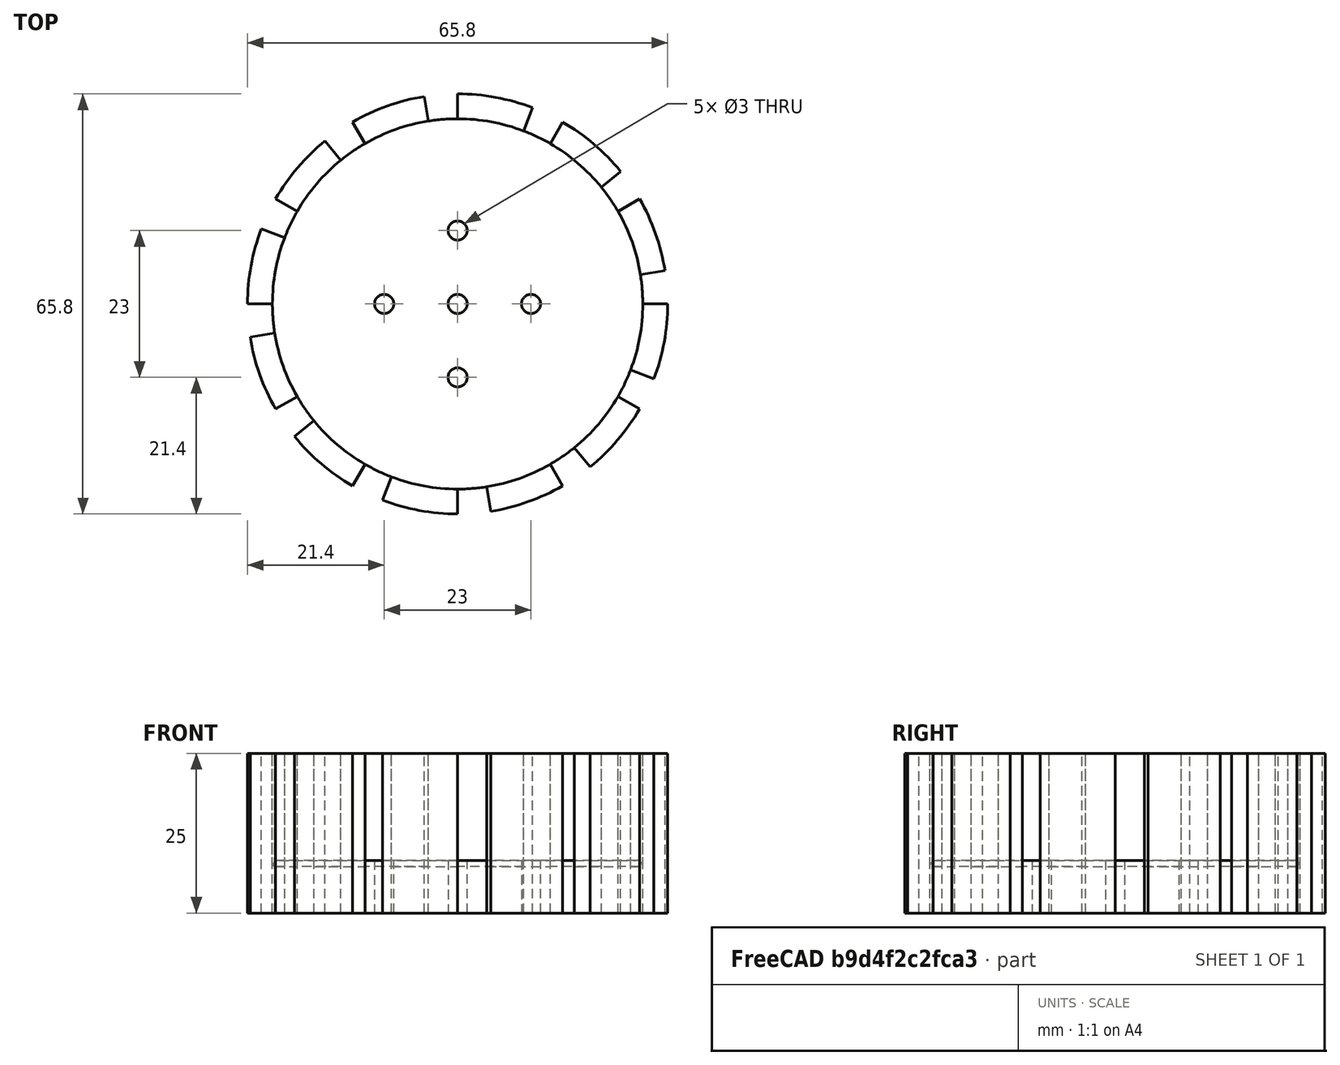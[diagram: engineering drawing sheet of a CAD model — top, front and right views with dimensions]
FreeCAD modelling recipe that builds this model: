
FCSTD DOCUMENT  (FreeCAD 1.0R39109 (Git))
Label: wheel
License: CERN Open Hardware Licence weakly-reciprocal
LicenseURL: https://cern-ohl.web.cern.ch/
objects: TechDraw::DrawViewDimension×3, Sketcher::SketchObject×2, PartDesign::Pad×2, PartDesign::Body×2, TechDraw::DrawProjGroupItem×2, TechDraw::DrawSVGTemplate×1, TechDraw::DrawViewImage×1, PartDesign::Fillet×1, PartDesign::Boolean×1, App::Part×1, TechDraw::DrawProjGroup×1, TechDraw::DrawViewSection×1, TechDraw::DrawPage×1
note: 20 computed .brp shape members not serialized (recipe doc carries the construction recipe); baked Part::Feature solids carry a one-line shape summary decoded from their .brp

FEATURE [Sketcher::SketchObject] Sketch
  ArcFitTolerance = 1e-06
  AttachmentSupport = -> [XY_Plane001]
  FullyConstrained = true
  MakeInternals = false
  MapMode = 5
  sketch-geometry (10):
    g0: Circle CenterX=0 CenterY=0 CenterZ=0 NormalX=0 NormalY=0 NormalZ=1 AngleXU=0 Radius=29
    g1: Circle CenterX=0 CenterY=0 CenterZ=0 NormalX=0 NormalY=0 NormalZ=1 AngleXU=0 Radius=1.5
    g2: LineSegment [constr] StartX=0 StartY=0 StartZ=0 EndX=0 EndY=11.5 EndZ=0
    g3: LineSegment [constr] StartX=0 StartY=0 StartZ=0 EndX=11.5 EndY=0 EndZ=0
    g4: LineSegment [constr] StartX=0 StartY=0 StartZ=0 EndX=0 EndY=-11.5 EndZ=0
    g5: LineSegment [constr] StartX=0 StartY=0 StartZ=0 EndX=-11.5 EndY=0 EndZ=0
    g6: Circle CenterX=0 CenterY=11.5 CenterZ=0 NormalX=0 NormalY=0 NormalZ=1 AngleXU=0 Radius=1.5
    g7: Circle CenterX=11.5 CenterY=0 CenterZ=0 NormalX=0 NormalY=0 NormalZ=1 AngleXU=0 Radius=1.5
    g8: Circle CenterX=0 CenterY=-11.5 CenterZ=0 NormalX=0 NormalY=0 NormalZ=1 AngleXU=0 Radius=1.5
    g9: Circle CenterX=-11.5 CenterY=0 CenterZ=0 NormalX=0 NormalY=0 NormalZ=1 AngleXU=0 Radius=1.5
  constraints (26):
    c: Coincident(g0,g-1)
    c: Coincident(g1,g0)
    c: Diameter(g0) = 58
    c: Diameter(g1) = 3
    c: Block(g0)
    c: Block(g1)
    c: Coincident(g2,g0)
    c: PointOnObject(g2,g-2)
    c: Coincident(g3,g0)
    c: PointOnObject(g3,g-1)
    c: Coincident(g4,g0)
    c: PointOnObject(g4,g-2)
    c: Coincident(g5,g0)
    c: PointOnObject(g5,g-1)
    c: Equal(g5,g2)
    c: Equal(g3,g2)
    c: Equal(g4,g2)
    c: DistanceX(g5,g5) = 11.5
    c: Diameter(g6) = 3
    c: Coincident(g6,g2)
    c: Diameter(g7) = 3
    c: Coincident(g7,g3)
    c: Diameter(g8) = 3
    c: Coincident(g8,g4)
    c: Diameter(g9) = 3
    c: Coincident(g9,g5)
FEATURE [PartDesign::Pad] Pad
  Direction = (0,0,1)
  Length = 8.25
  Length2 = 10
  Profile = -> Sketch
  ReferenceAxis = -> Sketch [N_Axis]
  Suppressed = false
  Type = 0
FEATURE [Sketcher::SketchObject] Sketch004
  ArcFitTolerance = 1e-06
  FullyConstrained = false
  MakeInternals = false
  MapMode = 5
  sketch-geometry (50):
    g0: Circle [constr] CenterX=0 CenterY=0 CenterZ=0 NormalX=0 NormalY=0 NormalZ=1 AngleXU=0 Radius=32.9
    g1: Circle [constr] CenterX=0 CenterY=0 CenterZ=0 NormalX=0 NormalY=0 NormalZ=1 AngleXU=0 Radius=29
    g2: ArcOfCircle CenterX=0 CenterY=9.7e-15 CenterZ=0 NormalX=0 NormalY=0 NormalZ=1 AngleXU=0 Radius=32.9 StartAngle=5.91825 EndAngle=6.28319
    g3: ArcOfCircle CenterX=0 CenterY=9.7e-15 CenterZ=0 NormalX=0 NormalY=0 NormalZ=1 AngleXU=0 Radius=29 StartAngle=5.91825 EndAngle=6.28319
    g4: LineSegment StartX=29 StartY=-2.32e-14 StartZ=0 EndX=32.9 EndY=-2.32e-14 EndZ=0
    g5: LineSegment StartX=27.0903 StartY=-10.3497 StartZ=0 EndX=30.7335 EndY=-11.7415 EndZ=0
    g6: ArcOfCircle CenterX=-3.69141e-06 CenterY=0 CenterZ=0 NormalX=0 NormalY=0 NormalZ=1 AngleXU=0 Radius=29 StartAngle=0.158668 EndAngle=0.523599
    g7: LineSegment StartX=25.1147 StartY=14.5 StartZ=0 EndX=28.4922 EndY=16.45 EndZ=0
    g8: ArcOfCircle CenterX=-3.69141e-06 CenterY=0 CenterZ=0 NormalX=0 NormalY=0 NormalZ=1 AngleXU=0 Radius=32.9 StartAngle=0.158668 EndAngle=0.523599
    g9: LineSegment StartX=28.6357 StartY=4.58208 StartZ=0 EndX=32.4867 EndY=5.1983 EndZ=0
    g10: ArcOfCircle CenterX=0 CenterY=7.38281e-06 CenterZ=0 NormalX=0 NormalY=0 NormalZ=1 AngleXU=0 Radius=29 StartAngle=0.682267 EndAngle=1.0472
    g11: LineSegment StartX=14.5 StartY=25.1147 StartZ=0 EndX=16.45 EndY=28.4922 EndZ=0
    g12: ArcOfCircle CenterX=0 CenterY=7.38281e-06 CenterZ=0 NormalX=0 NormalY=0 NormalZ=1 AngleXU=0 Radius=32.9 StartAngle=0.682266 EndAngle=1.0472
    g13: LineSegment StartX=22.5082 StartY=18.2861 StartZ=0 EndX=25.5352 EndY=20.7452 EndZ=0
    g14: ArcOfCircle CenterX=0 CenterY=1.755e-12 CenterZ=0 NormalX=0 NormalY=0 NormalZ=1 AngleXU=0 Radius=29 StartAngle=1.20587 EndAngle=1.5708
    g15: LineSegment StartX=9.47705e-06 StartY=29 StartZ=0 EndX=1.07516e-05 EndY=32.9 EndZ=0
    g16: ArcOfCircle CenterX=0 CenterY=1.755e-12 CenterZ=0 NormalX=0 NormalY=0 NormalZ=1 AngleXU=0 Radius=32.9 StartAngle=1.20587 EndAngle=1.5708
    g17: LineSegment StartX=10.3497 StartY=27.0903 StartZ=0 EndX=11.7415 EndY=30.7335 EndZ=0
    g18: ArcOfCircle CenterX=0 CenterY=1.68437e-06 CenterZ=0 NormalX=0 NormalY=0 NormalZ=1 AngleXU=0 Radius=29 StartAngle=1.72946 EndAngle=2.0944
    g19: LineSegment StartX=-14.5 StartY=25.1147 StartZ=0 EndX=-16.45 EndY=28.4922 EndZ=0
    g20: ArcOfCircle CenterX=0 CenterY=1.68437e-06 CenterZ=0 NormalX=0 NormalY=0 NormalZ=1 AngleXU=0 Radius=32.9 StartAngle=1.72946 EndAngle=2.0944
    g21: LineSegment StartX=-4.58208 StartY=28.6357 StartZ=0 EndX=-5.1983 EndY=32.4867 EndZ=0
    g22: ArcOfCircle CenterX=-2.15492e-07 CenterY=0 CenterZ=0 NormalX=0 NormalY=0 NormalZ=1 AngleXU=0 Radius=29 StartAngle=2.25306 EndAngle=2.61799
    g23: LineSegment StartX=-25.1147 StartY=14.5 StartZ=0 EndX=-28.4922 EndY=16.45 EndZ=0
    g24: ArcOfCircle CenterX=-2.15492e-07 CenterY=0 CenterZ=0 NormalX=0 NormalY=0 NormalZ=1 AngleXU=0 Radius=32.9 StartAngle=2.25306 EndAngle=2.61799
    g25: LineSegment StartX=-18.2861 StartY=22.5082 StartZ=0 EndX=-20.7452 EndY=25.5352 EndZ=0
    g26: ArcOfCircle CenterX=0 CenterY=0 CenterZ=0 NormalX=0 NormalY=0 NormalZ=1 AngleXU=0 Radius=29 StartAngle=2.77666 EndAngle=3.14159
    g27: LineSegment StartX=-29 StartY=1.124e-12 StartZ=0 EndX=-32.9 EndY=4e-15 EndZ=0
    g28: ArcOfCircle CenterX=0 CenterY=0 CenterZ=0 NormalX=0 NormalY=0 NormalZ=1 AngleXU=0 Radius=32.9 StartAngle=2.77666 EndAngle=3.14159
    g29: LineSegment StartX=-27.0903 StartY=10.3497 StartZ=0 EndX=-30.7335 EndY=11.7415 EndZ=0
    g30: ArcOfCircle CenterX=2.48829e-06 CenterY=0 CenterZ=0 NormalX=0 NormalY=0 NormalZ=1 AngleXU=0 Radius=29 StartAngle=3.30026 EndAngle=3.66519
    g31: LineSegment StartX=-25.1147 StartY=-14.5 StartZ=0 EndX=-28.4922 EndY=-16.45 EndZ=0
    g32: ArcOfCircle CenterX=2.48829e-06 CenterY=0 CenterZ=0 NormalX=0 NormalY=0 NormalZ=1 AngleXU=0 Radius=32.9 StartAngle=3.30026 EndAngle=3.66519
    g33: LineSegment StartX=-28.6357 StartY=-4.58208 StartZ=0 EndX=-32.4867 EndY=-5.1983 EndZ=0
    g34: ArcOfCircle CenterX=0 CenterY=-2.15491e-07 CenterZ=0 NormalX=0 NormalY=0 NormalZ=1 AngleXU=0 Radius=29 StartAngle=3.82386 EndAngle=4.18879
    g35: LineSegment StartX=-14.5 StartY=-25.1147 StartZ=0 EndX=-16.45 EndY=-28.4922 EndZ=0
    g36: ArcOfCircle CenterX=0 CenterY=-2.15491e-07 CenterZ=0 NormalX=0 NormalY=0 NormalZ=1 AngleXU=0 Radius=32.9 StartAngle=3.82386 EndAngle=4.18879
    g37: LineSegment StartX=-22.5082 StartY=-18.2861 StartZ=0 EndX=-25.5352 EndY=-20.7452 EndZ=0
    g38: ArcOfCircle CenterX=0 CenterY=0 CenterZ=0 NormalX=0 NormalY=0 NormalZ=1 AngleXU=0 Radius=29 StartAngle=4.34746 EndAngle=4.71239
    g39: LineSegment StartX=-5.3e-15 StartY=-29 StartZ=0 EndX=6.45344e-07 EndY=-32.9 EndZ=0
    g40: ArcOfCircle CenterX=0 CenterY=0 CenterZ=0 NormalX=0 NormalY=0 NormalZ=1 AngleXU=0 Radius=32.9 StartAngle=4.34746 EndAngle=4.71239
    g41: LineSegment StartX=-10.3497 StartY=-27.0903 StartZ=0 EndX=-11.7415 EndY=-30.7335 EndZ=0
    g42: ArcOfCircle CenterX=0 CenterY=0 CenterZ=0 NormalX=0 NormalY=0 NormalZ=1 AngleXU=0 Radius=29 StartAngle=4.87106 EndAngle=5.23599
    g43: LineSegment StartX=14.5 StartY=-25.1147 StartZ=0 EndX=16.45 EndY=-28.4922 EndZ=0
    g44: ArcOfCircle CenterX=0 CenterY=0 CenterZ=0 NormalX=0 NormalY=0 NormalZ=1 AngleXU=0 Radius=32.9 StartAngle=4.87106 EndAngle=5.23599
    g45: LineSegment StartX=4.58208 StartY=-28.6357 StartZ=0 EndX=5.1983 EndY=-32.4867 EndZ=0
    g46: ArcOfCircle CenterX=0 CenterY=-7.74437e-06 CenterZ=0 NormalX=0 NormalY=0 NormalZ=1 AngleXU=0 Radius=29 StartAngle=5.39466 EndAngle=5.75959
    g47: LineSegment StartX=25.1147 StartY=-14.5 StartZ=0 EndX=28.4922 EndY=-16.45 EndZ=0
    g48: ArcOfCircle CenterX=0 CenterY=-7.74437e-06 CenterZ=0 NormalX=0 NormalY=0 NormalZ=1 AngleXU=0 Radius=32.9 StartAngle=5.39466 EndAngle=5.75959
    g49: LineSegment StartX=18.2861 StartY=-22.5082 StartZ=0 EndX=20.7452 EndY=-25.5352 EndZ=0
  constraints (82):
    c: Coincident(g0,g-1)
    c: Coincident(g1,g0)
    c: Diameter(g1) = 58
    c: Diameter(g0) = 65.8
    c: Radius(g2) = 32.9
    c: Angle(g2) = 0.364931
    c: PointOnObject(g2,g-2)
    c: PointOnObject(g2,g0)
    c: Angle(g3) = 0.364931
    c: Coincident(g3,g2)
    c: PointOnObject(g3,g1)
    c: Coincident(g4,g3)
    c: Coincident(g4,g2)
    c: Horizontal(g4)
    c: Coincident(g5,g3)
    c: Coincident(g5,g2)
    c: Equal(g2,g8)
    c: Equal(g2,g12)
    c: Equal(g2,g16)
    c: Equal(g2,g20)
    c: Equal(g2,g24)
    c: Equal(g2,g28)
    c: Equal(g2,g32)
    c: Equal(g2,g36)
    c: Equal(g2,g40)
    c: Equal(g2,g44)
    c: Equal(g2,g48)
    c: Coincident(g6,g8)
    c: Coincident(g10,g12)
    c: Coincident(g14,g16)
    c: Coincident(g18,g20)
    c: Coincident(g22,g24)
    c: Coincident(g26,g28)
    c: Coincident(g30,g32)
    c: Coincident(g34,g36)
    c: Coincident(g38,g40)
    c: Coincident(g42,g44)
    c: Coincident(g46,g48)
    c: Coincident(g7,g6)
    c: Coincident(g11,g10)
    c: Coincident(g15,g14)
    c: Coincident(g19,g18)
    c: Coincident(g23,g22)
    c: Coincident(g27,g26)
    c: Coincident(g31,g30)
    c: Coincident(g35,g34)
    c: Coincident(g39,g38)
    c: Coincident(g43,g42)
    c: Coincident(g47,g46)
    c: Coincident(g7,g8)
    c: Coincident(g11,g12)
    c: Coincident(g15,g16)
    c: Coincident(g19,g20)
    c: Coincident(g23,g24)
    c: Coincident(g27,g28)
    c: Coincident(g31,g32)
    c: Coincident(g35,g36)
    c: Coincident(g39,g40)
    c: Coincident(g43,g44)
    c: Coincident(g47,g48)
    c: Coincident(g9,g6)
    c: Coincident(g13,g10)
    c: Coincident(g17,g14)
    c: Coincident(g21,g18)
    c: Coincident(g25,g22)
    c: Coincident(g29,g26)
    c: Coincident(g33,g30)
    c: Coincident(g37,g34)
    c: Coincident(g41,g38)
    c: Coincident(g45,g42)
    c: Coincident(g49,g46)
    c: Coincident(g9,g8)
    c: Coincident(g13,g12)
    c: Coincident(g17,g16)
    c: Coincident(g21,g20)
    c: Coincident(g25,g24)
    c: Coincident(g29,g28)
    c: Coincident(g33,g32)
    c: Coincident(g37,g36)
    c: Coincident(g41,g40)
    c: Coincident(g45,g44)
    c: Coincident(g49,g48)
FEATURE [PartDesign::Pad] Pad004
  Direction = (0,0,1)
  Length = 25
  Length2 = 10
  Profile = -> Sketch004
  ReferenceAxis = -> Sketch004 [N_Axis]
  Suppressed = false
  Type = 0
FEATURE [PartDesign::Body] Body004
  AllowCompound = true
  Group = -> [Sketch004,Pad004]
  Origin = -> Origin006
  Tip = -> Pad004
FEATURE [TechDraw::DrawSVGTemplate] Template  label="テンプレート"
  Height = 210
  Orientation = 1
  Template = <path>
  Width = 297
FEATURE [TechDraw::DrawViewImage] ActiveView  label="アクティブビュー"
  Height = 102.4
  ImageFile = <userpath>/.cache/FreeCAD/Cache/FreeCAD_Doc_5c669459-2d2e-4c9e-9a0c-683f5f23e2a7_ddc12d_923242/PageActiveViewMOpqH5.png
  LockPosition = false
  Rotation = 0
  ScaleType = 2
  Width = 128
  X = 210.968
  Y = 80.6247
FEATURE [PartDesign::Fillet] Fillet
  Base = -> Pad [Edge3]
  BaseFeature = -> Pad
  Radius = 1
  SupportTransform = false
  Suppressed = false
  UseAllEdges = false
FEATURE [PartDesign::Boolean] Boolean
  BaseFeature = -> Fillet
  Group = -> [Body004]
  Suppressed = false
  Type = 0
  UsePlacement = true
FEATURE [PartDesign::Body] Body
  AllowCompound = false
  Group = -> [Sketch,Pad,Fillet,Boolean]
  Origin = -> Origin001
  Tip = -> Boolean
FEATURE [App::Part] Part  label="wheel"
  Group = -> [Body]
  Origin = -> Origin
FEATURE [TechDraw::DrawProjGroupItem] View  label="上面"
  CoarseView = false
  Direction = (-1e-16,1e-16,1)
  Focus = 100
  HardHidden = false
  IsoCount = 0
  IsoHidden = false
  IsoVisible = false
  LockPosition = true
  Perspective = false
  Rotation = 0
  RotationVector = (1,0,0)
  ScaleType = 2
  ScrubCount = 1
  SeamHidden = false
  SeamVisible = false
  SmoothHidden = false
  SmoothVisible = true
  Source = -> [Part]
  Type = 0
  X = 0
  XDirection = (0,1,-1e-16)
  Y = 0
FEATURE [TechDraw::DrawProjGroupItem] ProjItem001  label="左面"
  CoarseView = false
  Direction = (0,-1,2e-16)
  Focus = 100
  HardHidden = false
  IsoCount = 0
  IsoHidden = false
  IsoVisible = false
  LockPosition = false
  Perspective = false
  Rotation = 0
  RotationVector = (1,0,0)
  ScaleType = 0
  ScrubCount = 1
  SeamHidden = false
  SeamVisible = false
  SmoothHidden = false
  SmoothVisible = true
  Source = -> [Part]
  Type = 1
  X = 65.4
  XDirection = (-1e-16,2e-16,1)
  Y = 0
FEATURE [TechDraw::DrawProjGroup] ProjGroup
  Anchor = -> View
  AutoDistribute = true
  LockPosition = false
  ProjectionType = 0
  Rotation = 0
  ScaleType = 0
  Source = -> [Part]
  Views = -> [View,ProjItem001]
  X = 55.7374
  Y = 62.6978
  spacingX = 20
  spacingY = 20
FEATURE [TechDraw::DrawViewDimension] Dimension  label="寸法"
  AngleOverride = false
  Arbitrary = false
  ArbitraryTolerances = false
  BoxCorners = (2) [(-32.9,-32.9,0),(32.9,32.9,0)]
  EqualTolerance = true
  ExtensionAngle = 0
  FormatSpec = ⌀%.2w
  FormatSpecOverTolerance = %+.2w
  FormatSpecUnderTolerance = %+.2w
  Inverted = false
  LineAngle = 0
  LockPosition = false
  MeasureType = 1
  OverTolerance = 0
  References2D = -> [View]
  Rotation = 0
  ScaleType = 0
  TheoreticalExact = false
  Type = 5
  UnderTolerance = 0
  X = -9.24264
  Y = 11.9621
FEATURE [TechDraw::DrawViewDimension] Dimension001  label="寸法001"
  AngleOverride = false
  Arbitrary = false
  ArbitraryTolerances = false
  BoxCorners = (2) [(-32.9,-32.9,0),(32.9,32.9,0)]
  EqualTolerance = true
  ExtensionAngle = 0
  FormatSpec = ⌀%.2w
  FormatSpecOverTolerance = %+.2w
  FormatSpecUnderTolerance = %+.2w
  Inverted = false
  LineAngle = 0
  LockPosition = false
  MeasureType = 1
  OverTolerance = 0
  References2D = -> [View]
  Rotation = 0
  ScaleType = 0
  TheoreticalExact = false
  Type = 5
  UnderTolerance = 0
  X = -42.7154
  Y = 9.79245
FEATURE [TechDraw::DrawViewDimension] Dimension002  label="寸法002"
  AngleOverride = false
  Arbitrary = false
  ArbitraryTolerances = false
  BoxCorners = (2) [(-12.5,-32.9,-1e-07),(12.5,32.9,1e-07)]
  EqualTolerance = true
  ExtensionAngle = 0
  FormatSpec = %.2w
  FormatSpecOverTolerance = %+.2w
  FormatSpecUnderTolerance = %+.2w
  Inverted = false
  LineAngle = 0
  LockPosition = false
  MeasureType = 1
  OverTolerance = 0
  References2D = -> [ProjItem001]
  Rotation = 0
  ScaleType = 0
  TheoreticalExact = false
  Type = 1
  UnderTolerance = 0
  X = 0
  Y = 43.1664
FEATURE [TechDraw::DrawViewSection] SectionView  label="セクション 1 - 1"
  BaseView = -> View
  CoarseView = false
  CutSurfaceDisplay = 2
  Direction = (1,1e-16,1e-16)
  FileGeomPattern = <path>
  FileHatchPattern = <path>
  Focus = 100
  FuseBeforeCut = false
  HardHidden = false
  HatchOffset = (0,0,0)
  HatchRotation = 0
  HatchScale = 1
  IsoCount = 0
  IsoHidden = false
  IsoVisible = false
  LockPosition = false
  NameGeomPattern = Diamond
  Perspective = false
  Rotation = 0
  ScaleType = 0
  ScrubCount = 1
  SeamHidden = false
  SeamVisible = false
  SectionDirection = 4
  SectionLineStretch = 1
  SectionNormal = (1,1e-16,1e-16)
  SectionOrigin = (0,0,12.5)
  SectionSymbol = 1
  SmoothHidden = false
  SmoothVisible = true
  Source = -> [Part]
  TrimAfterCut = false
  UsePreviousCut = false
  X = 55.5308
  XDirection = (-1e-16,1,-1e-16)
  Y = 131.845
FEATURE [TechDraw::DrawPage] Page  label="用紙"
  KeepUpdated = true
  NextBalloonIndex = 1
  ProjectionType = 0
  Template = -> Template
  Views = -> [ActiveView,ProjGroup,SectionView,Dimension,Dimension001,Dimension002]
note: 3 file-system paths scrubbed to <path> (originals preserved in the JSON sidecar)
